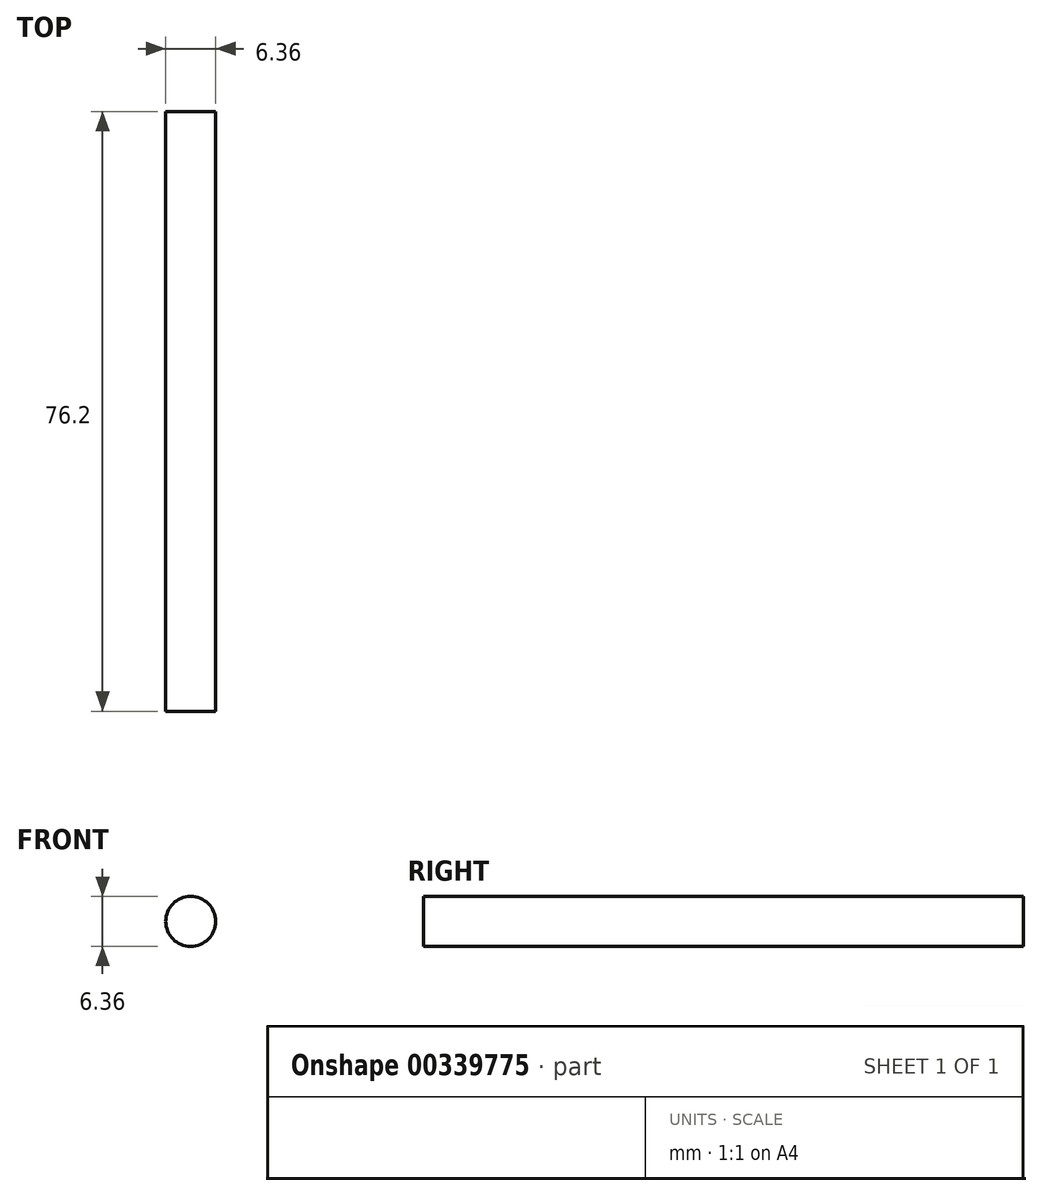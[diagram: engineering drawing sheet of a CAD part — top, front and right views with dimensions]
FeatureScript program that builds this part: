
annotation { "Feature Type Name" : "Feature", "Feature Type Description" : "" }
export const myFeature = defineFeature(function(context is Context, id is Id, definition is map)
    precondition{}
    {
        {
            var Q0;
            Q0=qCreatedBy(makeId("Front.planeOp"),FACE);
            var sketch = newSketch(context, id + "F0", { "sketchPlane" : qUnion([Q0])});
            skCircle(sketch, "E0", {"center": v(0, 0) * mm, "radius": 3.18 * mm});
            skSolve(sketch);
        }
        {
            var Q0;
            Q0=qSketchRegion(id+"F0",true);
            extrude(context, id + "F1", {"entities" : qUnion([Q0]), "oppositeDirection" : true, "depth" : 76.2 * mm});
        }
    });
